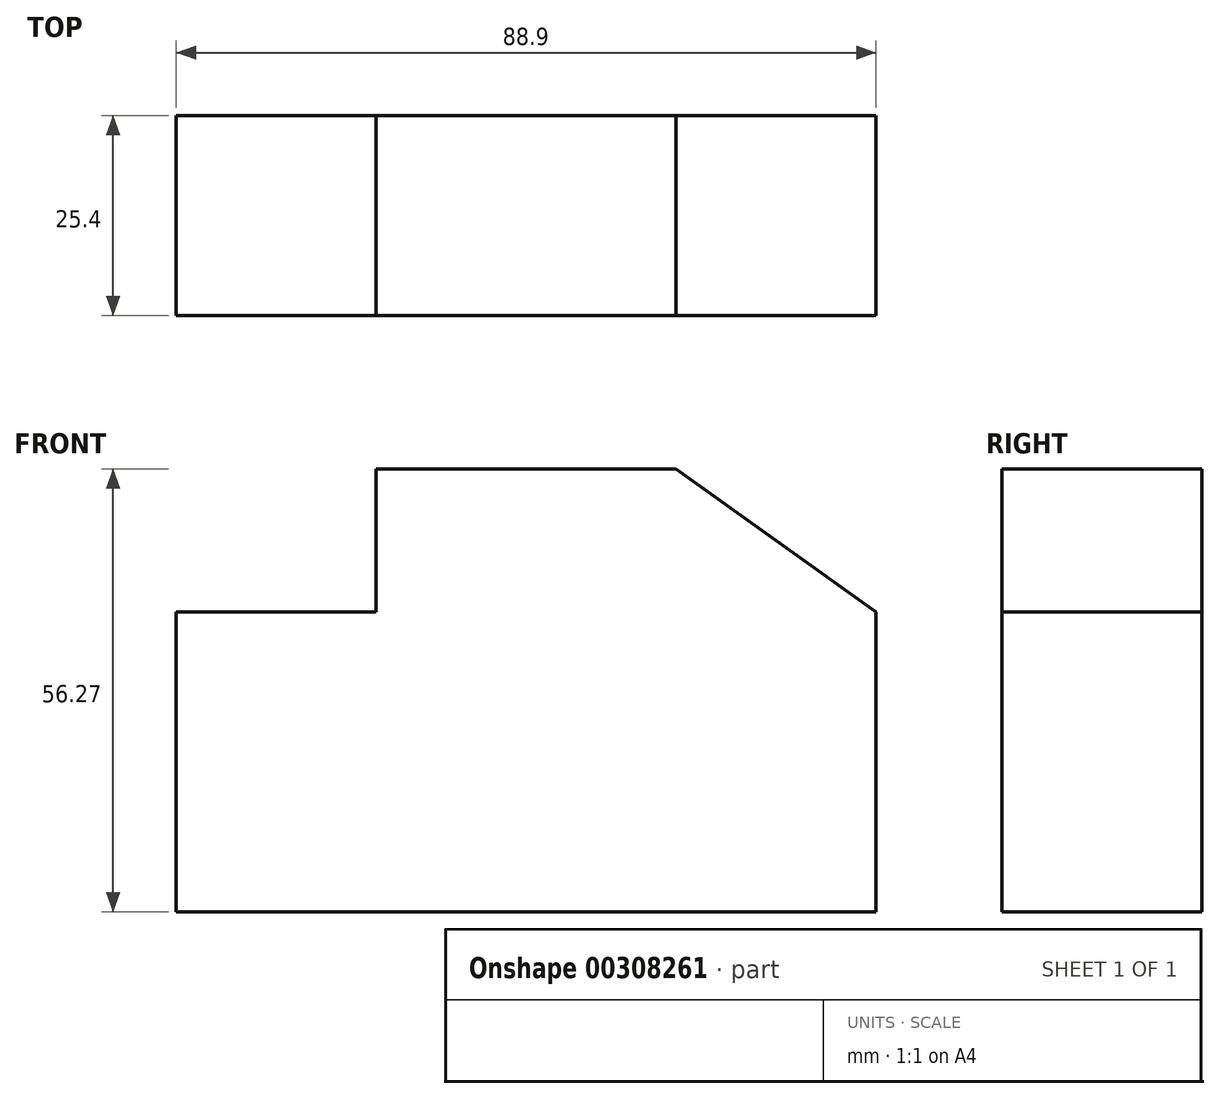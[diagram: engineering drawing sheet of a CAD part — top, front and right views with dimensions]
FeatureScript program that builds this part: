
annotation { "Feature Type Name" : "Feature", "Feature Type Description" : "" }
export const myFeature = defineFeature(function(context is Context, id is Id, definition is map)
    precondition{}
    {
        {
            var Q0;
            Q0=qCreatedBy(makeId("Front.planeOp"),FACE);
            var sketch = newSketch(context, id + "F0", { "sketchPlane" : qUnion([Q0])});
            skLineSegment(sketch, "E0", {"start": v(-39.84, -21.33) * mm, "end": v(49.06, -21.33) * mm});
            skLineSegment(sketch, "E1", {"start": v(49.06, -21.33) * mm, "end": v(49.06, 16.77) * mm});
            skLineSegment(sketch, "E2", {"start": v(49.06, 16.77) * mm, "end": v(23.66, 34.94) * mm});
            skLineSegment(sketch, "E3", {"start": v(23.66, 34.94) * mm, "end": v(-14.44, 34.94) * mm});
            skLineSegment(sketch, "E4", {"start": v(-14.44, 34.94) * mm, "end": v(-14.44, 16.77) * mm});
            skLineSegment(sketch, "E5", {"start": v(-14.44, 16.77) * mm, "end": v(-39.84, 16.77) * mm});
            skLineSegment(sketch, "E6", {"start": v(-39.84, 16.77) * mm, "end": v(-39.84, -21.33) * mm});
            skSolve(sketch);
        }
        {
            var Q0;
            Q0=makeQuery(id+"F0.imprint","IMPRINT",FACE,{"disambiguationData":[TD([[makeQuery(id+"F0.imprint","IMPRINT",EDGE,{"derivedFrom":sQuery(id+"F0.wireOp",EDGE,"E0")}),1.0]])]});
            extrude(context, id + "F1", {"entities" : qUnion([Q0]), "depth" : 25.4 * mm});
        }
    });
